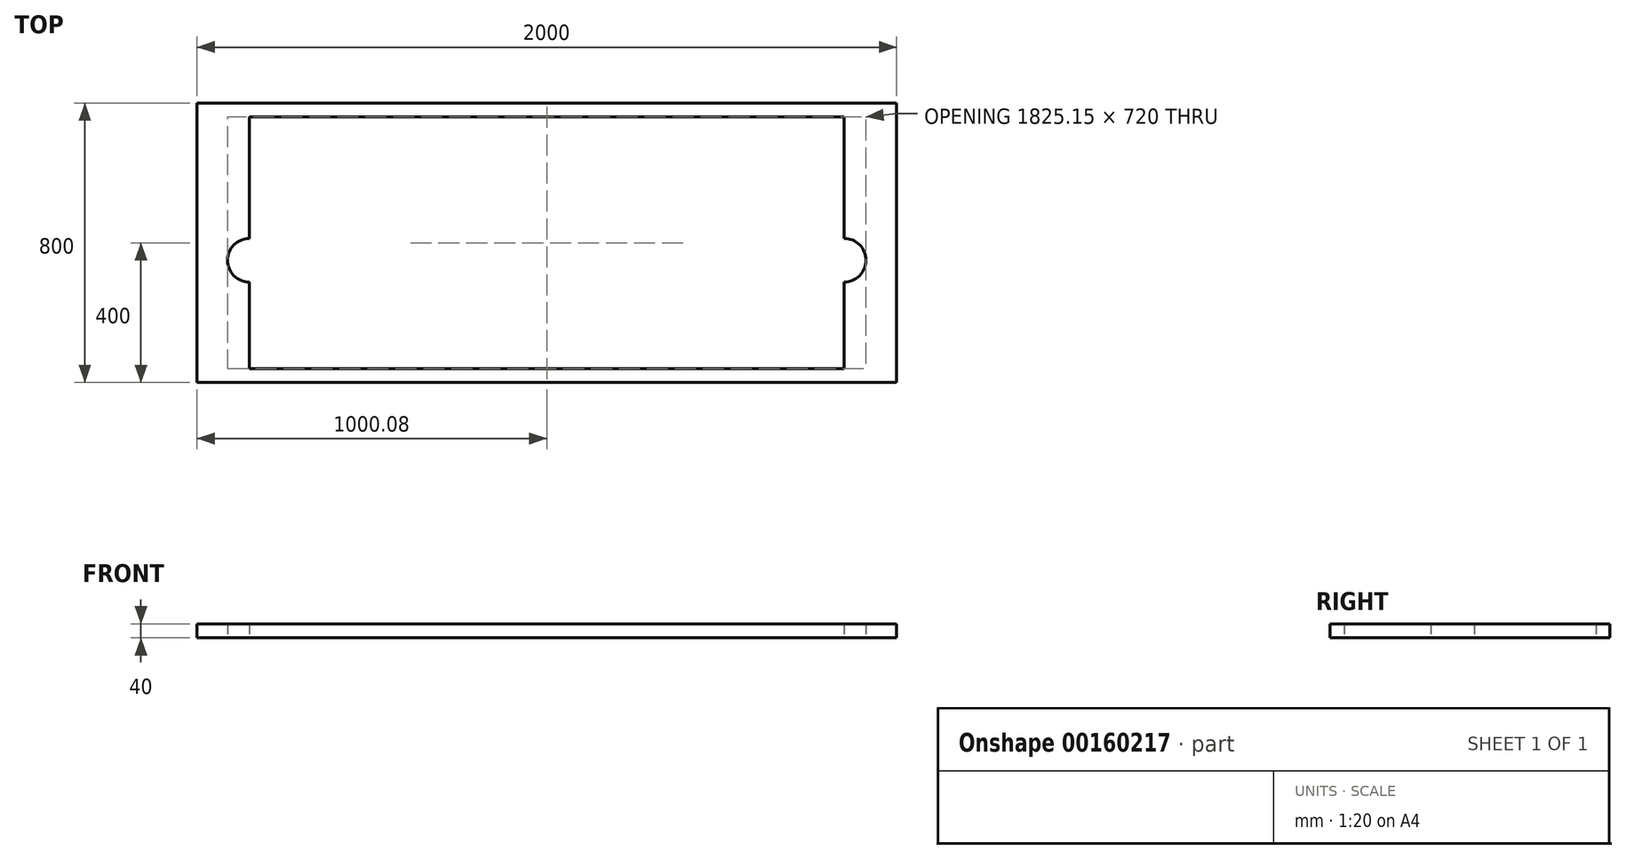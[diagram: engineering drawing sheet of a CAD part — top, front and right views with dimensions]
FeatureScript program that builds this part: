
annotation { "Feature Type Name" : "Feature", "Feature Type Description" : "" }
export const myFeature = defineFeature(function(context is Context, id is Id, definition is map)
    precondition{}
    {
        {
            var Q0;
            Q0=qCreatedBy(makeId("Top.planeOp"),FACE);
            var sketch = newSketch(context, id + "F0", { "sketchPlane" : qUnion([Q0])});
            skLineSegment(sketch, "E0.bottom", {"start": v(-1000, -400) * mm, "end": v(1000, -400) * mm});
            skLineSegment(sketch, "E0.top", {"start": v(-1000, 400) * mm, "end": v(1000, 400) * mm});
            skLineSegment(sketch, "E0.left", {"start": v(-1000, -400) * mm, "end": v(-1000, 400) * mm});
            skLineSegment(sketch, "E0.right", {"start": v(1000, -400) * mm, "end": v(1000, 400) * mm});
            skPoint(sketch, "E0.middle", {"position": v(0, 0) * mm});
            skLineSegment(sketch, "E1.bottom", {"start": v(-850, -360) * mm, "end": v(850, -360) * mm});
            skLineSegment(sketch, "E1.top", {"start": v(-850, 360) * mm, "end": v(850, 360) * mm});
            skLineSegment(sketch, "E1.left", {"start": v(-850, -360) * mm, "end": v(-850, -112.5) * mm});
            skLineSegment(sketch, "E1.right", {"start": v(850, -360) * mm, "end": v(850, -112.65) * mm});
            skArc(sketch, "E2", {"start": v(-850, -112.5) * mm, "mid": v(-912.5, -50) * mm, "end": v(-850, 12.5) * mm});
            skArc(sketch, "E3", {"start": v(850, -112.65) * mm, "mid": v(912.65, -50) * mm, "end": v(850, 12.65) * mm});
            skLineSegment(sketch, "E4.trimOffspring", {"start": v(-850, 12.5) * mm, "end": v(-850, 360) * mm});
            skLineSegment(sketch, "E5.trimOffspring", {"start": v(850, 12.65) * mm, "end": v(850, 360) * mm});
            skSolve(sketch);
        }
        {
            var Q0;
            Q0 = qSketchRegion(id + "F0", true);
            extrude(context, id + "F1", {"entities" : qUnion([Q0]), "depth" : 40 * mm});
        }
    });
